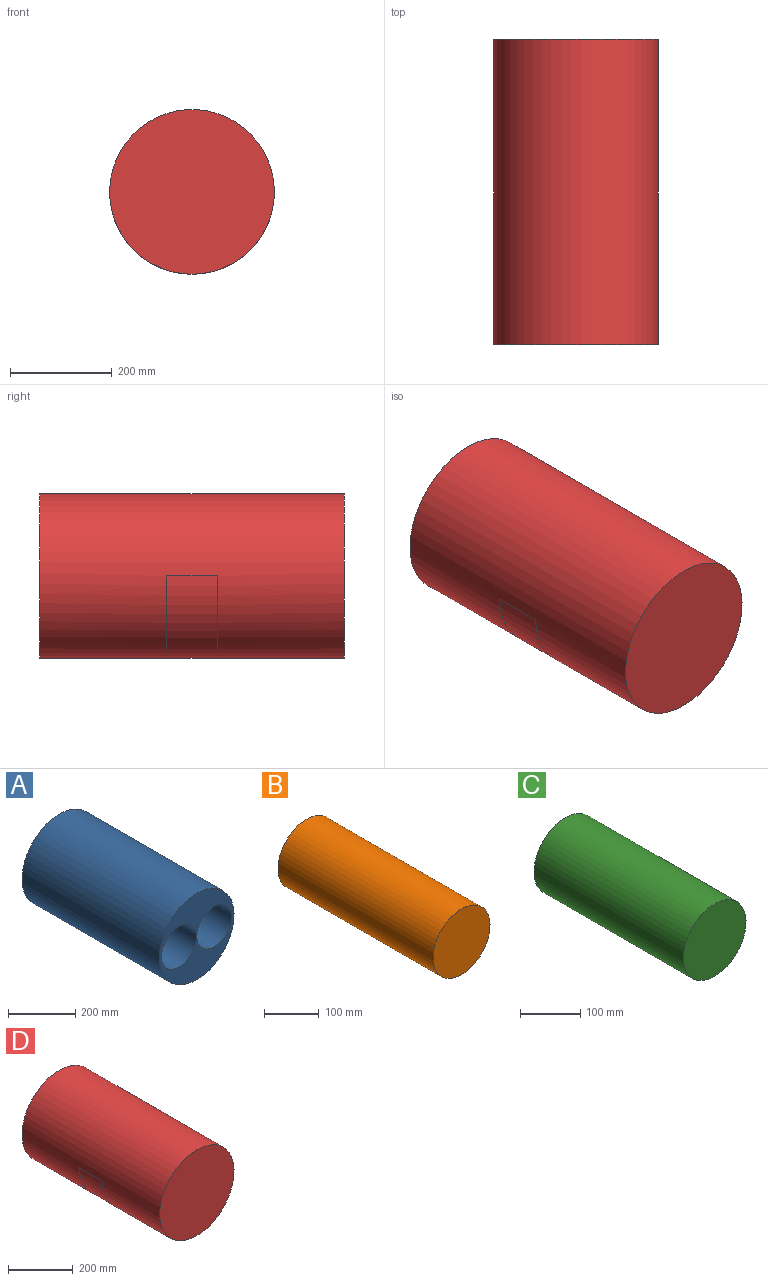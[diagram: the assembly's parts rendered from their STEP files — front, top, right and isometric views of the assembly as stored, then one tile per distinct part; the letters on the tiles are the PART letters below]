
ASSEMBLY  parts=4 mates=3
PART A: 5 faces, bbox 314x576x314 mm
  f0: cylinder r=73.5mm len=576mm, axis (0,1,0), area 266004.9mm2, adj f3,f4
  f1: cylinder r=73.5mm len=576mm, axis (0,1,0), area 266004.9mm2, adj f3,f4
  f2: cylinder r=157mm len=576mm, axis (0,1,0), area 568201mm2, adj f3,f4
  f3: plane 314x314mm, normal (0,-1,0), area 43493.8mm2, adj f0,f1,f2
  f4: plane 314x314mm, normal (0,1,0), area 43493.8mm2, adj f0,f1,f2
PART B: 3 faces, bbox 147x400x147 mm
  f0: cylinder r=73.5mm len=400mm, axis (0,1,0), area 184725.6mm2, adj f1,f2
  f1: plane 147x147mm, normal (0,-1,0), area 16971.7mm2, adj f0
  f2: plane 147x147mm, normal (0,1,0), area 16971.7mm2, adj f0
PART C: 3 faces, bbox 147x350x147 mm
  f0: cylinder r=73.5mm len=350mm, axis (0,1,0), area 161634.9mm2, adj f1,f2
  f1: plane 147x147mm, normal (0,-1,0), area 16971.7mm2, adj f0
  f2: plane 147x147mm, normal (0,1,0), area 16971.7mm2, adj f0
PART D: 11 faces, bbox 324.2x600x324.1 mm
  f0: cylinder r=162mm len=600mm, axis (0,1,0), area 559831.8mm2, adj f1,f2,f3,f4,f5,f6
  f1: plane 324x324mm, normal (0,-1,0), area 82448mm2, adj f0
  f2: plane 324x324mm, normal (0,1,0), area 82448mm2, adj f0
  f3: plane 324.2x162.1mm, normal (0,1,0), area 50.9mm2, adj f0,f4,f6,f7
  f4: plane 100x0.1mm, normal (0,0,1), area 10mm2, adj f0,f3,f5,f7
  f5: plane 324.2x162.1mm, normal (0,-1,0), area 50.9mm2, adj f0,f4,f6,f7
  f6: plane 100x0.1mm, normal (0,0,1), area 10mm2, adj f0,f3,f5,f7
  f7: cylinder r=162.1mm len=324.2mm, axis (0,-1,0), area 50925.2mm2, adj f3,f4,f5,f6
  f8: cylinder r=157mm len=576mm, axis (0,-1,0), area 568201mm2, adj f9,f10
  f9: plane 314x314mm, normal (0,-1,0), area 77437.1mm2, adj f8
  f10: plane 314x314mm, normal (0,1,0), area 77437.1mm2, adj f8
PLACE A at identity
PLACE B t=(-74.5,0,0)mm
PLACE C t=(74.5,0,0)mm
PLACE D at identity
MATE fastened C.f0 <-> A.f1  axis (0,-1,0) through (74.5,-175,0)mm
MATE fastened D.f8 <-> A.f2  axis (0,1,0) through (0,-288,0)mm
MATE fastened B.f0 <-> A.f0  axis (0,-1,0) through (-74.5,-200,0)mm
